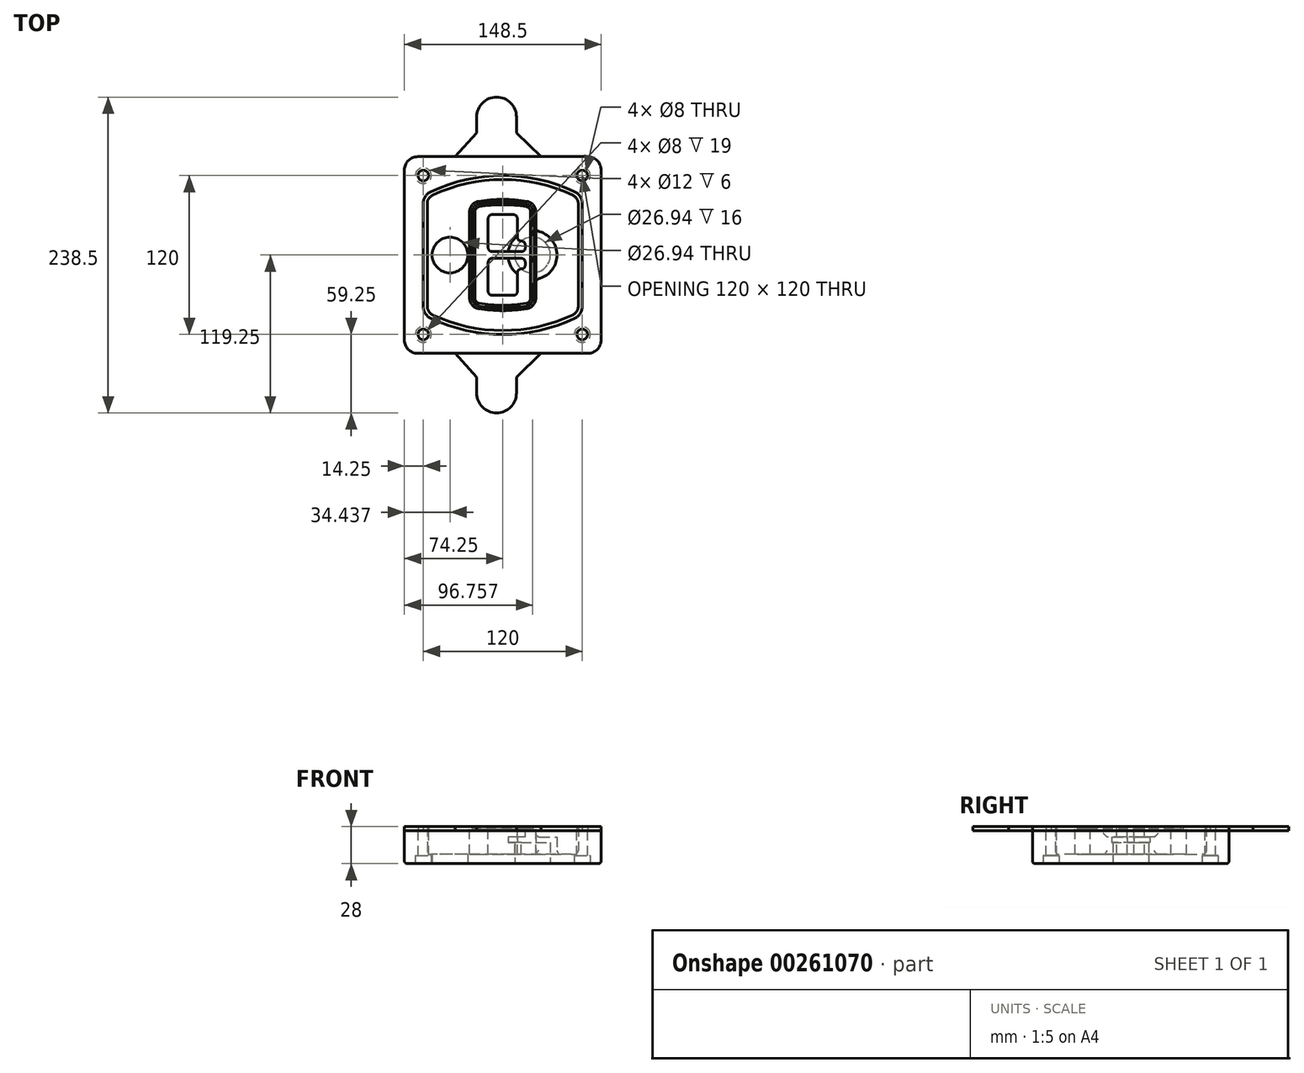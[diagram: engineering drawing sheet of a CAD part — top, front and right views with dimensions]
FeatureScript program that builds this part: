
annotation { "Feature Type Name" : "Feature", "Feature Type Description" : "" }
export const myFeature = defineFeature(function(context is Context, id is Id, definition is map)
    precondition{}
    {
        {
            var Q0;
            Q0=qCreatedBy(makeId("Top.planeOp"),FACE);
            var sketch = newSketch(context, id + "F0", { "sketchPlane" : qUnion([Q0])});
            skPoint(sketch, "E0.rect.middle", {"position": v(0, 0) * mm});
            skLineSegment(sketch, "E1.bottom", {"start": v(-64.25, -74.25) * mm, "end": v(64.25, -74.25) * mm});
            skLineSegment(sketch, "E1.top", {"start": v(-64.25, 74.25) * mm, "end": v(64.25, 74.25) * mm});
            skLineSegment(sketch, "E1.left", {"start": v(-74.25, -64.25) * mm, "end": v(-74.25, 64.25) * mm});
            skLineSegment(sketch, "E1.right", {"start": v(74.25, -64.25) * mm, "end": v(74.25, 64.25) * mm});
            skLineSegment(sketch, "E2", {"start": v(-74.25, 74.25) * mm, "end": v(74.25, -74.25) * mm, "construction": true});
            skLineSegment(sketch, "E3", {"start": v(74.25, 74.25) * mm, "end": v(-74.25, -74.25) * mm, "construction": true});
            skCircle(sketch, "E4", {"center": v(-60, 60) * mm, "radius": 4 * mm});
            skCircle(sketch, "E5", {"center": v(60, 60) * mm, "radius": 4 * mm});
            skCircle(sketch, "E6", {"center": v(60, -60) * mm, "radius": 4 * mm});
            skCircle(sketch, "E7", {"center": v(-60, -60) * mm, "radius": 4 * mm});
            skLineSegment(sketch, "E8", {"start": v(-60, 60) * mm, "end": v(60, 60) * mm, "construction": true});
            skLineSegment(sketch, "E9", {"start": v(60, 60) * mm, "end": v(60, -60) * mm, "construction": true});
            skLineSegment(sketch, "E10", {"start": v(60, -60) * mm, "end": v(-60, -60) * mm, "construction": true});
            skLineSegment(sketch, "E11", {"start": v(-60, -60) * mm, "end": v(-60, 60) * mm, "construction": true});
            skLineSegment(sketch, "E12", {"start": v(-60, 38.83) * mm, "end": v(-60, -38.83) * mm});
            skLineSegment(sketch, "E13", {"start": v(60, 38.83) * mm, "end": v(60, -38.83) * mm});
            skArc(sketch, "E14", {"start": v(54.26, 47.88) * mm, "mid": v(0, 60) * mm, "end": v(-54.26, 47.88) * mm});
            skArc(sketch, "E15", {"start": v(-54.26, -47.88) * mm, "mid": v(0, -60) * mm, "end": v(54.26, -47.88) * mm});
            skLineSegment(sketch, "E16", {"start": v(-60, 0) * mm, "end": v(60, 0) * mm, "construction": true});
            skPoint(sketch, "E17.visualSharp", {"position": v(-60, -45) * mm});
            skArc(sketch, "E17.filletArc", {"start": v(-60, -38.83) * mm, "mid": v(-58.44, -44.2) * mm, "end": v(-54.26, -47.88) * mm});
            skPoint(sketch, "E18.visualSharp", {"position": v(-60, 45) * mm});
            skArc(sketch, "E18.filletArc", {"start": v(-54.26, 47.88) * mm, "mid": v(-58.44, 44.2) * mm, "end": v(-60, 38.83) * mm});
            skPoint(sketch, "E19.visualSharp", {"position": v(60, 45) * mm});
            skArc(sketch, "E19.filletArc", {"start": v(60, 38.83) * mm, "mid": v(58.44, 44.2) * mm, "end": v(54.26, 47.88) * mm});
            skPoint(sketch, "E20.visualSharp", {"position": v(60, -45) * mm});
            skArc(sketch, "E20.filletArc", {"start": v(54.26, -47.88) * mm, "mid": v(58.44, -44.2) * mm, "end": v(60, -38.83) * mm});
            skPoint(sketch, "E21.visualSharp", {"position": v(-74.25, 74.25) * mm});
            skArc(sketch, "E21.filletArc", {"start": v(-64.25, 74.25) * mm, "mid": v(-71.32, 71.32) * mm, "end": v(-74.25, 64.25) * mm});
            skPoint(sketch, "E22.visualSharp", {"position": v(74.25, 74.25) * mm});
            skArc(sketch, "E22.filletArc", {"start": v(74.25, 64.25) * mm, "mid": v(71.32, 71.32) * mm, "end": v(64.25, 74.25) * mm});
            skPoint(sketch, "E23.visualSharp", {"position": v(74.25, -74.25) * mm});
            skArc(sketch, "E23.filletArc", {"start": v(64.25, -74.25) * mm, "mid": v(71.32, -71.32) * mm, "end": v(74.25, -64.25) * mm});
            skPoint(sketch, "E24.visualSharp", {"position": v(-74.25, -74.25) * mm});
            skArc(sketch, "E24.filletArc", {"start": v(-74.25, -64.25) * mm, "mid": v(-71.32, -71.32) * mm, "end": v(-64.25, -74.25) * mm});
            skArc(sketch, "E25.0", {"start": v(57, 38.83) * mm, "mid": v(55.9, 42.58) * mm, "end": v(52.98, 45.17) * mm});
            skLineSegment(sketch, "E25.1", {"start": v(57, 38.83) * mm, "end": v(57, -38.83) * mm});
            skArc(sketch, "E25.2", {"start": v(52.98, -45.17) * mm, "mid": v(55.9, -42.58) * mm, "end": v(57, -38.83) * mm});
            skArc(sketch, "E25.3", {"start": v(-52.98, -45.17) * mm, "mid": v(0, -57) * mm, "end": v(52.98, -45.17) * mm});
            skArc(sketch, "E25.4", {"start": v(-57, -38.83) * mm, "mid": v(-55.9, -42.58) * mm, "end": v(-52.98, -45.17) * mm});
            skArc(sketch, "E25.5", {"start": v(52.98, 45.17) * mm, "mid": v(0, 57) * mm, "end": v(-52.98, 45.17) * mm});
            skLineSegment(sketch, "E25.6", {"start": v(-57, 38.83) * mm, "end": v(-57, -38.83) * mm});
            skArc(sketch, "E25.7", {"start": v(-52.98, 45.17) * mm, "mid": v(-55.9, 42.58) * mm, "end": v(-57, 38.83) * mm});
            skArc(sketch, "E26.0", {"start": v(-55.96, 51.5) * mm, "mid": v(-61.82, 46.33) * mm, "end": v(-64, 38.83) * mm});
            skArc(sketch, "E26.1", {"start": v(55.96, 51.5) * mm, "mid": v(0, 64) * mm, "end": v(-55.96, 51.5) * mm});
            skArc(sketch, "E26.2", {"start": v(64, 38.83) * mm, "mid": v(61.82, 46.33) * mm, "end": v(55.96, 51.5) * mm});
            skLineSegment(sketch, "E26.3", {"start": v(64, 38.83) * mm, "end": v(64, -38.83) * mm});
            skArc(sketch, "E26.4", {"start": v(55.96, -51.5) * mm, "mid": v(61.82, -46.33) * mm, "end": v(64, -38.83) * mm});
            skLineSegment(sketch, "E26.5", {"start": v(-64, 38.83) * mm, "end": v(-64, -38.83) * mm});
            skArc(sketch, "E26.6", {"start": v(-55.96, -51.5) * mm, "mid": v(0, -64) * mm, "end": v(55.96, -51.5) * mm});
            skArc(sketch, "E26.7", {"start": v(-64, -38.83) * mm, "mid": v(-61.82, -46.33) * mm, "end": v(-55.96, -51.5) * mm});
            skSolve(sketch);
        }
        {
            var Q0;
            Q0=makeQuery(id+"F0.imprint","IMPRINT",FACE,{"disambiguationData":[TD([[makeQuery(id+"F0.imprint","IMPRINT",EDGE,{"derivedFrom":sQuery(id+"F0.wireOp",EDGE,"E1.bottom")}),1.0]])]});
            var Q1;
            Q1=makeQuery(id+"F0.imprint","IMPRINT",FACE,{"disambiguationData":[TD([[makeQuery(id+"F0.imprint","IMPRINT",EDGE,{"derivedFrom":sQuery(id+"F0.wireOp",EDGE,"E12")}),1.0]])]});
            var Q2;
            Q2=makeQuery(id+"F0.imprint","IMPRINT",FACE,{"disambiguationData":[TD([[makeQuery(id+"F0.imprint","IMPRINT",EDGE,{"derivedFrom":sQuery(id+"F0.wireOp",EDGE,"E25.0")}),1.0]])]});
            var Q3;
            Q3=makeQuery(id+"F0.imprint","IMPRINT",FACE,{"disambiguationData":[TD([[makeQuery(id+"F0.imprint","IMPRINT",EDGE,{"derivedFrom":sQuery(id+"F0.wireOp",EDGE,"E12")}),-1.0]])]});
            extrude(context, id + "F1", {"entities" : qUnion([Q0, Q1, Q2, Q3]), "oppositeDirection" : true, "depth" : 25 * mm});
        }
        {
            var Q0;
            Q0=makeQuery(id+"F0.imprint","IMPRINT",FACE,{"disambiguationData":[TD([[makeQuery(id+"F0.imprint","IMPRINT",EDGE,{"derivedFrom":sQuery(id+"F0.wireOp",EDGE,"E12")}),1.0]])]});
            extrude(context, id + "F2", {"entities" : qUnion([Q0]), "operationType" : NewBodyOperationType.ADD, "depth" : 3 * mm});
        }
        {
            var Q0;
            Q0=makeQuery(id+"F0.imprint","IMPRINT",FACE,{"disambiguationData":[TD([[makeQuery(id+"F0.imprint","IMPRINT",EDGE,{"derivedFrom":sQuery(id+"F0.wireOp",EDGE,"E25.0")}),1.0]])]});
            extrude(context, id + "F3", {"entities" : qUnion([Q0]), "operationType" : NewBodyOperationType.REMOVE, "oppositeDirection" : true, "depth" : 18 * mm});
        }
        {
            var Q0;
            Q0=makeQuery(id+"F2.opExtrude","CAP_FACE",FACE,{"disambiguationData":[OSD([sQuery(id+"F0.wireOp",EDGE,"E12"),sQuery(id+"F0.wireOp",EDGE,"E13"),sQuery(id+"F0.wireOp",EDGE,"E14"),sQuery(id+"F0.wireOp",EDGE,"E15"),sQuery(id+"F0.wireOp",EDGE,"E17.filletArc"),sQuery(id+"F0.wireOp",EDGE,"E18.filletArc"),sQuery(id+"F0.wireOp",EDGE,"E19.filletArc"),sQuery(id+"F0.wireOp",EDGE,"E20.filletArc"),sQuery(id+"F0.wireOp",EDGE,"E25.0"),sQuery(id+"F0.wireOp",EDGE,"E25.1"),sQuery(id+"F0.wireOp",EDGE,"E25.2"),sQuery(id+"F0.wireOp",EDGE,"E25.3"),sQuery(id+"F0.wireOp",EDGE,"E25.4"),sQuery(id+"F0.wireOp",EDGE,"E25.5"),sQuery(id+"F0.wireOp",EDGE,"E25.6"),sQuery(id+"F0.wireOp",EDGE,"E25.7")])],"isStart":false});
            var sketch = newSketch(context, id + "F4", { "sketchPlane" : qUnion([Q0])});
            skArc(sketch, "E27.0", {"start": v(-18.34, -40.45) * mm, "mid": v(0, -42) * mm, "end": v(18.34, -40.45) * mm});
            skArc(sketch, "E28.0", {"start": v(18.34, 40.45) * mm, "mid": v(0, 42) * mm, "end": v(-18.34, 40.45) * mm});
            skLineSegment(sketch, "E29", {"start": v(-25, 32.57) * mm, "end": v(-25, -32.57) * mm});
            skLineSegment(sketch, "E30", {"start": v(25, 32.57) * mm, "end": v(25, -32.57) * mm});
            skLineSegment(sketch, "E31", {"start": v(-25, 39.1) * mm, "end": v(25, 39.1) * mm, "construction": true});
            skLineSegment(sketch, "E32", {"start": v(-25, -39.1) * mm, "end": v(25, -39.1) * mm, "construction": true});
            skPoint(sketch, "E33.visualSharp", {"position": v(-25, 39.1) * mm});
            skArc(sketch, "E33.filletArc", {"start": v(-18.34, 40.45) * mm, "mid": v(-23.11, 37.73) * mm, "end": v(-25, 32.57) * mm});
            skPoint(sketch, "E34.visualSharp", {"position": v(25, 39.1) * mm});
            skArc(sketch, "E34.filletArc", {"start": v(25, 32.57) * mm, "mid": v(23.11, 37.73) * mm, "end": v(18.34, 40.45) * mm});
            skPoint(sketch, "E35.visualSharp", {"position": v(25, -39.1) * mm});
            skArc(sketch, "E35.filletArc", {"start": v(18.34, -40.45) * mm, "mid": v(23.11, -37.73) * mm, "end": v(25, -32.57) * mm});
            skPoint(sketch, "E36.visualSharp", {"position": v(-25, -39.1) * mm});
            skArc(sketch, "E36.filletArc", {"start": v(-25, -32.57) * mm, "mid": v(-23.11, -37.73) * mm, "end": v(-18.34, -40.45) * mm});
            skArc(sketch, "E37.0", {"start": v(52.98, 45.17) * mm, "mid": v(0, 57) * mm, "end": v(-52.98, 45.17) * mm});
            skArc(sketch, "E37.1", {"start": v(-52.98, 45.17) * mm, "mid": v(-55.9, 42.58) * mm, "end": v(-57, 38.83) * mm});
            skLineSegment(sketch, "E37.2", {"start": v(-57, 38.83) * mm, "end": v(-57, -38.83) * mm});
            skArc(sketch, "E37.3", {"start": v(-57, -38.83) * mm, "mid": v(-55.9, -42.58) * mm, "end": v(-52.98, -45.17) * mm});
            skArc(sketch, "E37.4", {"start": v(-52.98, -45.17) * mm, "mid": v(0, -57) * mm, "end": v(52.98, -45.17) * mm});
            skArc(sketch, "E37.5", {"start": v(52.98, -45.17) * mm, "mid": v(55.9, -42.58) * mm, "end": v(57, -38.83) * mm});
            skLineSegment(sketch, "E37.6", {"start": v(57, 38.83) * mm, "end": v(57, -38.83) * mm});
            skArc(sketch, "E37.7", {"start": v(57, 38.83) * mm, "mid": v(55.9, 42.58) * mm, "end": v(52.98, 45.17) * mm});
            skLineSegment(sketch, "E38.0", {"start": v(23, 32.57) * mm, "end": v(23, -32.57) * mm});
            skArc(sketch, "E38.1", {"start": v(18, -38.48) * mm, "mid": v(21.58, -36.44) * mm, "end": v(23, -32.57) * mm});
            skArc(sketch, "E38.2", {"start": v(-18, -38.48) * mm, "mid": v(0, -40) * mm, "end": v(18, -38.48) * mm});
            skArc(sketch, "E38.3", {"start": v(-23, -32.57) * mm, "mid": v(-21.58, -36.44) * mm, "end": v(-18, -38.48) * mm});
            skLineSegment(sketch, "E38.4", {"start": v(-23, 32.57) * mm, "end": v(-23, -32.57) * mm});
            skArc(sketch, "E38.5", {"start": v(23, 32.57) * mm, "mid": v(21.58, 36.44) * mm, "end": v(18, 38.48) * mm});
            skArc(sketch, "E38.6", {"start": v(-18, 38.48) * mm, "mid": v(-21.58, 36.44) * mm, "end": v(-23, 32.57) * mm});
            skArc(sketch, "E38.7", {"start": v(18, 38.48) * mm, "mid": v(0, 40) * mm, "end": v(-18, 38.48) * mm});
            skArc(sketch, "E39.0", {"start": v(21, 32.57) * mm, "mid": v(20.06, 35.15) * mm, "end": v(17.67, 36.5) * mm});
            skLineSegment(sketch, "E39.1", {"start": v(21, 32.57) * mm, "end": v(21, -32.57) * mm});
            skArc(sketch, "E39.2", {"start": v(17.67, -36.5) * mm, "mid": v(20.06, -35.15) * mm, "end": v(21, -32.57) * mm});
            skArc(sketch, "E39.3", {"start": v(-17.67, -36.5) * mm, "mid": v(0, -38) * mm, "end": v(17.67, -36.5) * mm});
            skArc(sketch, "E39.4", {"start": v(-21, -32.57) * mm, "mid": v(-20.06, -35.15) * mm, "end": v(-17.67, -36.5) * mm});
            skArc(sketch, "E39.5", {"start": v(17.67, 36.5) * mm, "mid": v(0, 38) * mm, "end": v(-17.67, 36.5) * mm});
            skLineSegment(sketch, "E39.6", {"start": v(-21, 32.57) * mm, "end": v(-21, -32.57) * mm});
            skArc(sketch, "E39.7", {"start": v(-17.67, 36.5) * mm, "mid": v(-20.06, 35.15) * mm, "end": v(-21, 32.57) * mm});
            skLineSegment(sketch, "E40", {"start": v(-25, 0) * mm, "end": v(25, 0) * mm, "construction": true});
            skLineSegment(sketch, "E41", {"start": v(-11, 5.5) * mm, "end": v(-11, 27.5) * mm});
            skLineSegment(sketch, "E42", {"start": v(-8, 30.5) * mm, "end": v(8, 30.5) * mm});
            skLineSegment(sketch, "E43", {"start": v(11, 27.5) * mm, "end": v(11, 13.5) * mm});
            skLineSegment(sketch, "E44", {"start": v(14, 10.5) * mm, "end": v(14, 10.5) * mm});
            skLineSegment(sketch, "E45", {"start": v(17, 7.5) * mm, "end": v(17, 5.5) * mm});
            skLineSegment(sketch, "E46", {"start": v(14, 2.5) * mm, "end": v(-8, 2.5) * mm});
            skPoint(sketch, "E47.visualSharp", {"position": v(-11, 30.5) * mm});
            skArc(sketch, "E47.filletArc", {"start": v(-8, 30.5) * mm, "mid": v(-10.12, 29.62) * mm, "end": v(-11, 27.5) * mm});
            skPoint(sketch, "E48.visualSharp", {"position": v(11, 30.5) * mm});
            skArc(sketch, "E48.filletArc", {"start": v(11, 27.5) * mm, "mid": v(10.12, 29.62) * mm, "end": v(8, 30.5) * mm});
            skPoint(sketch, "E49.visualSharp", {"position": v(11, 10.5) * mm});
            skArc(sketch, "E49.filletArc", {"start": v(11, 13.5) * mm, "mid": v(11.88, 11.38) * mm, "end": v(14, 10.5) * mm});
            skPoint(sketch, "E50.visualSharp", {"position": v(17, 10.5) * mm});
            skArc(sketch, "E50.filletArc", {"start": v(17, 7.5) * mm, "mid": v(16.12, 9.62) * mm, "end": v(14, 10.5) * mm});
            skPoint(sketch, "E51.visualSharp", {"position": v(17, 2.5) * mm});
            skArc(sketch, "E51.filletArc", {"start": v(14, 2.5) * mm, "mid": v(16.12, 3.38) * mm, "end": v(17, 5.5) * mm});
            skPoint(sketch, "E52.visualSharp", {"position": v(-11, 2.5) * mm});
            skArc(sketch, "E52.filletArc", {"start": v(-11, 5.5) * mm, "mid": v(-10.12, 3.38) * mm, "end": v(-8, 2.5) * mm});
            skLineSegment(sketch, "E53.0.MirrorCS", {"start": v(14, -2.5) * mm, "end": v(-8, -2.5) * mm});
            skArc(sketch, "E54.0.MirrorCS", {"start": v(-11, -5.5) * mm, "mid": v(-10.12, -3.38) * mm, "end": v(-8, -2.5) * mm});
            skLineSegment(sketch, "E55.0.MirrorCS", {"start": v(-11, -5.5) * mm, "end": v(-11, -27.5) * mm});
            skArc(sketch, "E56.0.MirrorCS", {"start": v(-8, -30.5) * mm, "mid": v(-10.12, -29.62) * mm, "end": v(-11, -27.5) * mm});
            skLineSegment(sketch, "E57.0.MirrorCS", {"start": v(-8, -30.5) * mm, "end": v(8, -30.5) * mm});
            skArc(sketch, "E58.0.MirrorCS", {"start": v(11, -27.5) * mm, "mid": v(10.12, -29.62) * mm, "end": v(8, -30.5) * mm});
            skLineSegment(sketch, "E59.0.MirrorCS", {"start": v(11, -27.5) * mm, "end": v(11, -13.5) * mm});
            skArc(sketch, "E60.0.MirrorCS", {"start": v(11, -13.5) * mm, "mid": v(11.88, -11.38) * mm, "end": v(14, -10.5) * mm});
            skArc(sketch, "E61.0.MirrorCS", {"start": v(17, -7.5) * mm, "mid": v(16.12, -9.62) * mm, "end": v(14, -10.5) * mm});
            skLineSegment(sketch, "E62.0.MirrorCS", {"start": v(17, -7.5) * mm, "end": v(17, -5.5) * mm});
            skArc(sketch, "E63.0.MirrorCS", {"start": v(14, -2.5) * mm, "mid": v(16.12, -3.38) * mm, "end": v(17, -5.5) * mm});
            skSolve(sketch);
        }
        {
            var Q0;
            Q0=makeQuery(id+"F4.imprint","IMPRINT",FACE,{"disambiguationData":[TD([[makeQuery(id+"F4.imprint","IMPRINT",EDGE,{"derivedFrom":sQuery(id+"F4.wireOp",EDGE,"E27.0")}),1.0]])]});
            var Q1;
            Q1=makeQuery(id+"F4.imprint","IMPRINT",FACE,{"disambiguationData":[TD([[makeQuery(id+"F4.imprint","IMPRINT",EDGE,{"derivedFrom":sQuery(id+"F4.wireOp",EDGE,"E38.0")}),-1.0]])]});
            var Q2;
            Q2=makeQuery(id+"F4.imprint","IMPRINT",FACE,{"disambiguationData":[TD([[makeQuery(id+"F4.imprint","IMPRINT",EDGE,{"derivedFrom":sQuery(id+"F4.wireOp",EDGE,"E39.0")}),1.0]])]});
            extrude(context, id + "F5", {"entities" : qUnion([Q0, Q1, Q2]), "operationType" : NewBodyOperationType.ADD, "endBound" : BoundingType.UP_TO_NEXT, "oppositeDirection" : true, "depth" : 25 * mm});
        }
        {
            var Q0;
            Q0=makeQuery(id+"F4.imprint","IMPRINT",FACE,{"disambiguationData":[TD([[makeQuery(id+"F4.imprint","IMPRINT",EDGE,{"derivedFrom":sQuery(id+"F4.wireOp",EDGE,"E38.0")}),-1.0]])]});
            extrude(context, id + "F6", {"entities" : qUnion([Q0]), "operationType" : NewBodyOperationType.REMOVE, "oppositeDirection" : true, "depth" : 2 * mm});
        }
        {
            var Q0;
            Q0=makeQuery(id+"F1.opExtrude","CAP_FACE",FACE,{"disambiguationData":[OSD([sQuery(id+"F0.wireOp",EDGE,"E1.bottom"),sQuery(id+"F0.wireOp",EDGE,"E1.top"),sQuery(id+"F0.wireOp",EDGE,"E1.left"),sQuery(id+"F0.wireOp",EDGE,"E1.right"),sQuery(id+"F0.wireOp",EDGE,"E4"),sQuery(id+"F0.wireOp",EDGE,"E5"),sQuery(id+"F0.wireOp",EDGE,"E6"),sQuery(id+"F0.wireOp",EDGE,"E7"),sQuery(id+"F0.wireOp",EDGE,"E21.filletArc"),sQuery(id+"F0.wireOp",EDGE,"E22.filletArc"),sQuery(id+"F0.wireOp",EDGE,"E23.filletArc"),sQuery(id+"F0.wireOp",EDGE,"E24.filletArc")])],"isStart":false});
            var sketch = newSketch(context, id + "F7", { "sketchPlane" : qUnion([Q0])});
            skCircle(sketch, "E64", {"center": v(22.5, 0) * mm, "radius": 13.47 * mm});
            skCircle(sketch, "E65", {"center": v(-39.81, 0) * mm, "radius": 13.47 * mm});
            skLineSegment(sketch, "E66", {"start": v(74.25, 0) * mm, "end": v(-74.25, 0) * mm});
            skCircle(sketch, "E67", {"center": v(22.5, 0) * mm, "radius": 18.47 * mm});
            skCircle(sketch, "E68", {"center": v(60, -60) * mm, "radius": 6 * mm});
            skCircle(sketch, "E69", {"center": v(-60, -60) * mm, "radius": 6 * mm});
            skCircle(sketch, "E70", {"center": v(-60, 60) * mm, "radius": 6 * mm});
            skCircle(sketch, "E71", {"center": v(60, 60) * mm, "radius": 6 * mm});
            skSolve(sketch);
        }
        {
            var Q0;
            {var subQ1=sQuery(id+"F7.wireOp",EDGE,"E66");var subQ4=sQuery(id+"F7.wireOp",EDGE,"E64");var subQ6=makeQuery(id+"F7.imprint","INTERSECT",VERTEX,{"disambiguationData":[OD(0.0)],"derivedFrom":[subQ4,subQ1]});Q0=makeQuery(id+"F7.imprint","IMPRINT",FACE,{"disambiguationData":[TD([[makeQuery(id+"F7.imprint","IMPRINT",EDGE,{"disambiguationData":[TD([[subQ6,-1.0]])],"derivedFrom":subQ4}),-1.0]])]});}
            var Q1;
            {var subQ0=sQuery(id+"F7.wireOp",EDGE,"E66");var subQ1=sQuery(id+"F7.wireOp",EDGE,"E64");var subQ3=makeQuery(id+"F7.imprint","INTERSECT",VERTEX,{"disambiguationData":[OD(0.0)],"derivedFrom":[subQ1,subQ0]});Q1=makeQuery(id+"F7.imprint","IMPRINT",FACE,{"disambiguationData":[TD([[makeQuery(id+"F7.imprint","IMPRINT",EDGE,{"disambiguationData":[TD([[subQ3,-1.0]])],"derivedFrom":subQ1}),1.0]])]});}
            var Q2;
            {var subQ0=sQuery(id+"F7.wireOp",EDGE,"E66");var subQ1=sQuery(id+"F7.wireOp",EDGE,"E64");var subQ3=makeQuery(id+"F7.imprint","INTERSECT",VERTEX,{"disambiguationData":[OD(0.0)],"derivedFrom":[subQ1,subQ0]});Q2=makeQuery(id+"F7.imprint","IMPRINT",FACE,{"disambiguationData":[TD([[makeQuery(id+"F7.imprint","IMPRINT",EDGE,{"disambiguationData":[TD([[subQ3,1.0]])],"derivedFrom":subQ1}),1.0]])]});}
            var Q3;
            {var subQ1=sQuery(id+"F7.wireOp",EDGE,"E66");var subQ4=sQuery(id+"F7.wireOp",EDGE,"E64");var subQ6=makeQuery(id+"F7.imprint","INTERSECT",VERTEX,{"disambiguationData":[OD(0.0)],"derivedFrom":[subQ4,subQ1]});Q3=makeQuery(id+"F7.imprint","IMPRINT",FACE,{"disambiguationData":[TD([[makeQuery(id+"F7.imprint","IMPRINT",EDGE,{"disambiguationData":[TD([[subQ6,1.0]])],"derivedFrom":subQ4}),-1.0]])]});}
            extrude(context, id + "F8", {"entities" : qUnion([Q0, Q1, Q2, Q3]), "operationType" : NewBodyOperationType.ADD, "oppositeDirection" : true, "depth" : 20 * mm});
        }
        {
            var Q0;
            {var subQ0=sQuery(id+"F7.wireOp",EDGE,"E66");var subQ1=sQuery(id+"F7.wireOp",EDGE,"E64");var subQ3=makeQuery(id+"F7.imprint","INTERSECT",VERTEX,{"disambiguationData":[OD(0.0)],"derivedFrom":[subQ1,subQ0]});Q0=makeQuery(id+"F7.imprint","IMPRINT",FACE,{"disambiguationData":[TD([[makeQuery(id+"F7.imprint","IMPRINT",EDGE,{"disambiguationData":[TD([[subQ3,-1.0]])],"derivedFrom":subQ1}),1.0]])]});}
            var Q1;
            {var subQ0=sQuery(id+"F7.wireOp",EDGE,"E66");var subQ1=sQuery(id+"F7.wireOp",EDGE,"E64");var subQ3=makeQuery(id+"F7.imprint","INTERSECT",VERTEX,{"disambiguationData":[OD(0.0)],"derivedFrom":[subQ1,subQ0]});Q1=makeQuery(id+"F7.imprint","IMPRINT",FACE,{"disambiguationData":[TD([[makeQuery(id+"F7.imprint","IMPRINT",EDGE,{"disambiguationData":[TD([[subQ3,1.0]])],"derivedFrom":subQ1}),1.0]])]});}
            extrude(context, id + "F9", {"entities" : qUnion([Q0, Q1]), "operationType" : NewBodyOperationType.REMOVE, "oppositeDirection" : true, "depth" : 16 * mm});
        }
        {
            var Q0;
            {var subQ0=sQuery(id+"F7.wireOp",EDGE,"E66");var subQ1=sQuery(id+"F7.wireOp",EDGE,"E65");var subQ3=makeQuery(id+"F7.imprint","INTERSECT",VERTEX,{"disambiguationData":[OD(0.0)],"derivedFrom":[subQ1,subQ0]});Q0=makeQuery(id+"F7.imprint","IMPRINT",FACE,{"disambiguationData":[TD([[makeQuery(id+"F7.imprint","IMPRINT",EDGE,{"disambiguationData":[TD([[subQ3,-1.0]])],"derivedFrom":subQ1}),1.0]])]});}
            var Q1;
            {var subQ0=sQuery(id+"F7.wireOp",EDGE,"E66");var subQ1=sQuery(id+"F7.wireOp",EDGE,"E65");var subQ3=makeQuery(id+"F7.imprint","INTERSECT",VERTEX,{"disambiguationData":[OD(0.0)],"derivedFrom":[subQ1,subQ0]});Q1=makeQuery(id+"F7.imprint","IMPRINT",FACE,{"disambiguationData":[TD([[makeQuery(id+"F7.imprint","IMPRINT",EDGE,{"disambiguationData":[TD([[subQ3,1.0]])],"derivedFrom":subQ1}),1.0]])]});}
            extrude(context, id + "F10", {"entities" : qUnion([Q0, Q1]), "operationType" : NewBodyOperationType.REMOVE, "oppositeDirection" : true, "depth" : 25 * mm});
        }
        {
            var Q0;
            Q0=makeQuery(id+"F7.imprint","IMPRINT",FACE,{"disambiguationData":[TD([[makeQuery(id+"F7.imprint","IMPRINT",EDGE,{"derivedFrom":sQuery(id+"F7.wireOp",EDGE,"E68")}),1.0]])]});
            var Q1;
            Q1=makeQuery(id+"F7.imprint","IMPRINT",FACE,{"disambiguationData":[TD([[makeQuery(id+"F7.imprint","IMPRINT",EDGE,{"derivedFrom":makeQuery(id+"F1.opExtrude","CAP_EDGE",EDGE,{"disambiguationData":[OSD([sQuery(id+"F0.wireOp",EDGE,"E5")])],"isStart":false})}),-1.0]])]});
            var Q2;
            Q2=makeQuery(id+"F7.imprint","IMPRINT",FACE,{"disambiguationData":[TD([[makeQuery(id+"F7.imprint","IMPRINT",EDGE,{"derivedFrom":sQuery(id+"F7.wireOp",EDGE,"E69")}),1.0]])]});
            var Q3;
            Q3=makeQuery(id+"F7.imprint","IMPRINT",FACE,{"disambiguationData":[TD([[makeQuery(id+"F7.imprint","IMPRINT",EDGE,{"derivedFrom":makeQuery(id+"F1.opExtrude","CAP_EDGE",EDGE,{"disambiguationData":[OSD([sQuery(id+"F0.wireOp",EDGE,"E4")])],"isStart":false})}),-1.0]])]});
            var Q4;
            Q4=makeQuery(id+"F7.imprint","IMPRINT",FACE,{"disambiguationData":[TD([[makeQuery(id+"F7.imprint","IMPRINT",EDGE,{"derivedFrom":sQuery(id+"F7.wireOp",EDGE,"E70")}),1.0]])]});
            var Q5;
            Q5=makeQuery(id+"F7.imprint","IMPRINT",FACE,{"disambiguationData":[TD([[makeQuery(id+"F7.imprint","IMPRINT",EDGE,{"derivedFrom":makeQuery(id+"F1.opExtrude","CAP_EDGE",EDGE,{"disambiguationData":[OSD([sQuery(id+"F0.wireOp",EDGE,"E7")])],"isStart":false})}),-1.0]])]});
            var Q6;
            Q6=makeQuery(id+"F7.imprint","IMPRINT",FACE,{"disambiguationData":[TD([[makeQuery(id+"F7.imprint","IMPRINT",EDGE,{"derivedFrom":sQuery(id+"F7.wireOp",EDGE,"E71")}),1.0]])]});
            var Q7;
            Q7=makeQuery(id+"F7.imprint","IMPRINT",FACE,{"disambiguationData":[TD([[makeQuery(id+"F7.imprint","IMPRINT",EDGE,{"derivedFrom":makeQuery(id+"F1.opExtrude","CAP_EDGE",EDGE,{"disambiguationData":[OSD([sQuery(id+"F0.wireOp",EDGE,"E6")])],"isStart":false})}),-1.0]])]});
            extrude(context, id + "F11", {"entities" : qUnion([Q0, Q1, Q2, Q3, Q4, Q5, Q6, Q7]), "operationType" : NewBodyOperationType.REMOVE, "oppositeDirection" : true, "depth" : 6 * mm});
        }
        {
            var Q0;
            Q0=makeQuery(id+"F9.boolean.opBoolean","COPY",FACE,{"derivedFrom":makeQuery(id+"F9.opExtrude","CAP_FACE",FACE,{"disambiguationData":[OSD([sQuery(id+"F7.wireOp",EDGE,"E64")])],"isStart":false})});
            var sketch = newSketch(context, id + "F12", { "sketchPlane" : qUnion([Q0])});
            skArc(sketch, "E72.0", {"start": v(11, 14.45) * mm, "mid": v(6.45, 9.13) * mm, "end": v(4.2, 2.5) * mm});
            skArc(sketch, "E72.1", {"start": v(4.2, -2.5) * mm, "mid": v(6.45, -9.13) * mm, "end": v(11, -14.45) * mm});
            skLineSegment(sketch, "E73", {"start": v(4.2, -2.5) * mm, "end": v(14, -2.5) * mm});
            skLineSegment(sketch, "E74.0", {"start": v(14, 2.5) * mm, "end": v(4.2, 2.5) * mm});
            skArc(sketch, "E74.1", {"start": v(14, 2.5) * mm, "mid": v(16.12, 3.38) * mm, "end": v(17, 5.5) * mm});
            skLineSegment(sketch, "E74.2", {"start": v(17, 7.5) * mm, "end": v(17, 5.5) * mm});
            skArc(sketch, "E74.3", {"start": v(17, 7.5) * mm, "mid": v(16.12, 9.62) * mm, "end": v(14, 10.5) * mm});
            skArc(sketch, "E74.4", {"start": v(11, 13.5) * mm, "mid": v(11.88, 11.38) * mm, "end": v(14, 10.5) * mm});
            skLineSegment(sketch, "E74.5", {"start": v(11, 14.45) * mm, "end": v(11, 13.5) * mm});
            skLineSegment(sketch, "E74.7", {"start": v(14, -2.5) * mm, "end": v(4.2, -2.5) * mm});
            skArc(sketch, "E74.8", {"start": v(14, -2.5) * mm, "mid": v(16.12, -3.38) * mm, "end": v(17, -5.5) * mm});
            skLineSegment(sketch, "E74.9", {"start": v(17, -7.5) * mm, "end": v(17, -5.5) * mm});
            skArc(sketch, "E74.10", {"start": v(17, -7.5) * mm, "mid": v(16.12, -9.62) * mm, "end": v(14, -10.5) * mm});
            skArc(sketch, "E74.11", {"start": v(11, -13.5) * mm, "mid": v(11.88, -11.38) * mm, "end": v(14, -10.5) * mm});
            skLineSegment(sketch, "E74.12", {"start": v(11, -14.45) * mm, "end": v(11, -13.5) * mm});
            skPoint(sketch, "E75.orphan", {"position": v(11, -27.5) * mm});
            skPoint(sketch, "E76.orphan", {"position": v(-8, -2.5) * mm});
            skPoint(sketch, "E77.orphan", {"position": v(-8, 2.5) * mm});
            skPoint(sketch, "E78.orphan", {"position": v(11, 27.5) * mm});
            skSolve(sketch);
        }
        {
            var Q0;
            {var subQ7=sQuery(id+"F12.wireOp",EDGE,"E72.0");var subQ14=sQuery(id+"F12.wireOp",EDGE,"E72.1");var subQ16=sQuery(id+"F12.wireOp",EDGE,"E74.1");var subQ18=sQuery(id+"F12.wireOp",EDGE,"E74.8");Q0=qUnion([makeQuery(id+"F12.imprint","IMPRINT",FACE,{"disambiguationData":[TD([[makeQuery(id+"F12.imprint","IMPRINT",EDGE,{"derivedFrom":subQ7}),1.0]])]}),makeQuery(id+"F12.imprint","IMPRINT",FACE,{"disambiguationData":[TD([[makeQuery(id+"F12.imprint","IMPRINT",EDGE,{"derivedFrom":subQ14}),1.0]])]}),makeQuery(id+"F12.imprint","IMPRINT",FACE,{"disambiguationData":[TD([[makeQuery(id+"F12.imprint","IMPRINT",EDGE,{"derivedFrom":subQ16}),1.0]])]}),makeQuery(id+"F12.imprint","IMPRINT",FACE,{"disambiguationData":[TD([[makeQuery(id+"F12.imprint","IMPRINT",EDGE,{"derivedFrom":subQ18}),-1.0]])]})]);}
            var Q1;
            Q1=makeQuery(id+"F5.boolean.opBoolean","SPLIT",FACE,{"disambiguationData":[TD([makeQuery(id+"F5.opExtrude","SWEPT_FACE",FACE,{"disambiguationData":[OSD([sQuery(id+"F4.wireOp",EDGE,"E41")])]})])],"derivedFrom":makeQuery(id+"F3.boolean.opBoolean","COPY",FACE,{"derivedFrom":makeQuery(id+"F3.opExtrude","CAP_FACE",FACE,{"disambiguationData":[OSD([sQuery(id+"F0.wireOp",EDGE,"E25.0"),sQuery(id+"F0.wireOp",EDGE,"E25.1"),sQuery(id+"F0.wireOp",EDGE,"E25.2"),sQuery(id+"F0.wireOp",EDGE,"E25.3"),sQuery(id+"F0.wireOp",EDGE,"E25.4"),sQuery(id+"F0.wireOp",EDGE,"E25.5"),sQuery(id+"F0.wireOp",EDGE,"E25.6"),sQuery(id+"F0.wireOp",EDGE,"E25.7")])],"isStart":false})})});
            extrude(context, id + "F13", {"entities" : qUnion([Q0]), "operationType" : NewBodyOperationType.REMOVE, "endBound" : BoundingType.UP_TO_SURFACE, "endBoundEntityFace" : qUnion([Q1]), "depth" : 25 * mm});
        }
        {
            var Q0;
            Q0=makeQuery(id+"F3.boolean.opBoolean","COPY",EDGE,{"derivedFrom":makeQuery(id+"F3.opExtrude","CAP_EDGE",EDGE,{"disambiguationData":[OSD([sQuery(id+"F0.wireOp",EDGE,"E25.6")])],"isStart":false})});
            var Q1;
            Q1=makeQuery(id+"F8.boolean.opBoolean","INTERSECT",EDGE,{"derivedFrom":[makeQuery(id+"F5.opExtrude","SWEPT_FACE",FACE,{"disambiguationData":[OSD([sQuery(id+"F4.wireOp",EDGE,"E30")])]}),makeQuery(id+"F8.opExtrude","CAP_FACE",FACE,{"disambiguationData":[OSD([sQuery(id+"F7.wireOp",EDGE,"E67")])],"isStart":false})]});
            var Q2;
            Q2=makeQuery(id+"F8.boolean.opBoolean","INTERSECT",EDGE,{"disambiguationData":[OD(1.0)],"derivedFrom":[makeQuery(id+"F5.opExtrude","SWEPT_FACE",FACE,{"disambiguationData":[OSD([sQuery(id+"F4.wireOp",EDGE,"E30")])]}),makeQuery(id+"F8.opExtrude","SWEPT_FACE",FACE,{"disambiguationData":[OSD([sQuery(id+"F7.wireOp",EDGE,"E67")])]})]});
            var Q3;
            {var subQ0=sQuery(id+"F4.wireOp",EDGE,"E30");Q3=makeQuery(id+"F8.boolean.opBoolean","SPLIT",EDGE,{"disambiguationData":[TD([makeQuery(id+"F5.opExtrude","SWEPT_FACE",FACE,{"disambiguationData":[OSD([sQuery(id+"F4.wireOp",EDGE,"E35.filletArc")])]})])],"derivedFrom":makeQuery(id+"F5.opExtrude","CAP_EDGE",EDGE,{"disambiguationData":[OSD([subQ0])],"isStart":false})});}
            var Q4;
            {var subQ0=sQuery(id+"F0.wireOp",EDGE,"E25.7");var subQ1=sQuery(id+"F0.wireOp",EDGE,"E25.1");var subQ2=sQuery(id+"F0.wireOp",EDGE,"E25.6");var subQ3=sQuery(id+"F0.wireOp",EDGE,"E25.5");var subQ4=sQuery(id+"F0.wireOp",EDGE,"E25.4");var subQ5=sQuery(id+"F0.wireOp",EDGE,"E25.0");var subQ6=sQuery(id+"F0.wireOp",EDGE,"E25.2");var subQ7=sQuery(id+"F0.wireOp",EDGE,"E25.3");Q4=makeQuery(id+"F8.boolean.opBoolean","INTERSECT",EDGE,{"derivedFrom":[makeQuery(id+"F5.boolean.opBoolean","SPLIT",FACE,{"disambiguationData":[TD([makeQuery(id+"F2.opExtrude","SWEPT_FACE",FACE,{"disambiguationData":[OSD([subQ5])]})])],"derivedFrom":makeQuery(id+"F3.boolean.opBoolean","COPY",FACE,{"derivedFrom":makeQuery(id+"F3.opExtrude","CAP_FACE",FACE,{"disambiguationData":[OSD([subQ5,subQ1,subQ6,subQ7,subQ4,subQ3,subQ2,subQ0])],"isStart":false})})}),makeQuery(id+"F8.opExtrude","SWEPT_FACE",FACE,{"disambiguationData":[OSD([sQuery(id+"F7.wireOp",EDGE,"E67")])]})]});}
            var Q5;
            Q5=makeQuery(id+"F8.boolean.opBoolean","INTERSECT",EDGE,{"disambiguationData":[OD(0.0)],"derivedFrom":[makeQuery(id+"F5.opExtrude","SWEPT_FACE",FACE,{"disambiguationData":[OSD([sQuery(id+"F4.wireOp",EDGE,"E30")])]}),makeQuery(id+"F8.opExtrude","SWEPT_FACE",FACE,{"disambiguationData":[OSD([sQuery(id+"F7.wireOp",EDGE,"E67")])]})]});
            fillet(context, id + "F14", {"entities" : qUnion([Q0, Q1, Q2, Q3, Q4, Q5]), "radius" : 3 * mm, "tangentPropagation" : true, "allowEdgeOverflow" : false});
        }
        {
            var Q0;
            Q0=makeQuery(id+"F1.opExtrude","CAP_EDGE",EDGE,{"disambiguationData":[OSD([sQuery(id+"F0.wireOp",EDGE,"E1.bottom")])],"isStart":false});
            fillet(context, id + "F15", {"entities" : qUnion([Q0]), "radius" : 2 * mm, "tangentPropagation" : true, "allowEdgeOverflow" : false});
        }
        {
            var Q0;
            {var subQ0=sQuery(id+"F0.wireOp",EDGE,"E22.filletArc");var subQ1=sQuery(id+"F0.wireOp",EDGE,"E7");var subQ2=sQuery(id+"F0.wireOp",EDGE,"E6");var subQ3=sQuery(id+"F0.wireOp",EDGE,"E5");var subQ4=sQuery(id+"F0.wireOp",EDGE,"E4");var subQ5=sQuery(id+"F0.wireOp",EDGE,"E1.bottom");var subQ6=sQuery(id+"F0.wireOp",EDGE,"E21.filletArc");var subQ7=sQuery(id+"F0.wireOp",EDGE,"E1.top");var subQ8=sQuery(id+"F0.wireOp",EDGE,"E1.left");var subQ9=sQuery(id+"F0.wireOp",EDGE,"E1.right");var subQ10=sQuery(id+"F0.wireOp",EDGE,"E23.filletArc");var subQ11=sQuery(id+"F0.wireOp",EDGE,"E24.filletArc");Q0=makeQuery(id+"F2.boolean.opBoolean","SPLIT",FACE,{"disambiguationData":[TD([makeQuery(id+"F1.opExtrude","SWEPT_FACE",FACE,{"disambiguationData":[OSD([subQ5])]})])],"derivedFrom":makeQuery(id+"F1.opExtrude","CAP_FACE",FACE,{"disambiguationData":[OSD([subQ5,subQ7,subQ8,subQ9,subQ4,subQ3,subQ2,subQ1,subQ6,subQ0,subQ10,subQ11])],"isStart":true})});}
            var sketch = newSketch(context, id + "F16", { "sketchPlane" : qUnion([Q0])});
            skSolve(sketch);
        }
        {
            var Q0;
            Q0=makeQuery(id+"F16.imprint","IMPRINT",FACE,{"disambiguationData":[TD([[makeQuery(id+"F16.imprint","IMPRINT",EDGE,{"derivedFrom":makeQuery(id+"F1.opExtrude","CAP_EDGE",EDGE,{"disambiguationData":[OSD([sQuery(id+"F0.wireOp",EDGE,"E1.bottom")])],"isStart":true})}),1.0]])]});
            var sketch = newSketch(context, id + "F17", { "sketchPlane" : qUnion([Q0])});
            skLineSegment(sketch, "E79", {"start": v(-36.51, 73.73) * mm, "end": v(-19.64, 92.25) * mm});
            skLineSegment(sketch, "E80", {"start": v(28.73, 74.22) * mm, "end": v(10.36, 92.25) * mm});
            skLineSegment(sketch, "E81", {"start": v(-19.64, 92.25) * mm, "end": v(-19.64, 104.25) * mm});
            skLineSegment(sketch, "E82", {"start": v(10.36, 92.25) * mm, "end": v(10.36, 104.25) * mm});
            skArc(sketch, "E83", {"start": v(10.36, 104.25) * mm, "mid": v(-4.64, 119.25) * mm, "end": v(-19.64, 104.25) * mm});
            skCircle(sketch, "E84", {"center": v(-4.64, 104.25) * mm, "radius": 6 * mm});
            skLineSegment(sketch, "E85", {"start": v(-74.8, 0) * mm, "end": v(75, 0) * mm, "construction": true});
            skLineSegment(sketch, "E86.MirrorCS", {"start": v(-19.64, -92.25) * mm, "end": v(-19.64, -104.25) * mm});
            skArc(sketch, "E87.MirrorCS", {"start": v(10.36, -104.25) * mm, "mid": v(-4.64, -119.25) * mm, "end": v(-19.64, -104.25) * mm});
            skLineSegment(sketch, "E88.MirrorCS", {"start": v(10.36, -92.25) * mm, "end": v(10.36, -104.25) * mm});
            skLineSegment(sketch, "E89.MirrorCS", {"start": v(28.73, -74.22) * mm, "end": v(10.36, -92.25) * mm});
            skLineSegment(sketch, "E90.MirrorCS", {"start": v(-36.51, -73.73) * mm, "end": v(-19.64, -92.25) * mm});
            skCircle(sketch, "E91.MirrorC", {"center": v(-4.64, -104.25) * mm, "radius": 6 * mm});
            skSolve(sketch);
        }
        {
            var Q0;
            Q0 = qSketchRegion(id + "F17", true);
            var Q1;
            {var subQ1=sQuery(id+"F17.wireOp",EDGE,"E81");Q1=makeQuery(id+"F17.imprint","IMPRINT",FACE,{"disambiguationData":[TD([[makeQuery(id+"F17.imprint","IMPRINT",EDGE,{"derivedFrom":subQ1}),-1.0]])]});}
            var Q2;
            Q2=makeQuery(id+"F16.imprint","IMPRINT",FACE,{"disambiguationData":[TD([[makeQuery(id+"F16.imprint","IMPRINT",EDGE,{"derivedFrom":makeQuery(id+"F1.opExtrude","CAP_EDGE",EDGE,{"disambiguationData":[OSD([sQuery(id+"F0.wireOp",EDGE,"E1.bottom")])],"isStart":true})}),1.0]])]});
            var Q3;
            {var subQ6=sQuery(id+"F17.wireOp",EDGE,"E86.MirrorCS");Q3=makeQuery(id+"F17.imprint","IMPRINT",FACE,{"disambiguationData":[TD([[makeQuery(id+"F17.imprint","IMPRINT",EDGE,{"derivedFrom":subQ6}),1.0]])]});}
            extrude(context, id + "F18", {"entities" : qUnion([Q0, Q1, Q2, Q3]), "depth" : 3 * mm});
        }
    });
